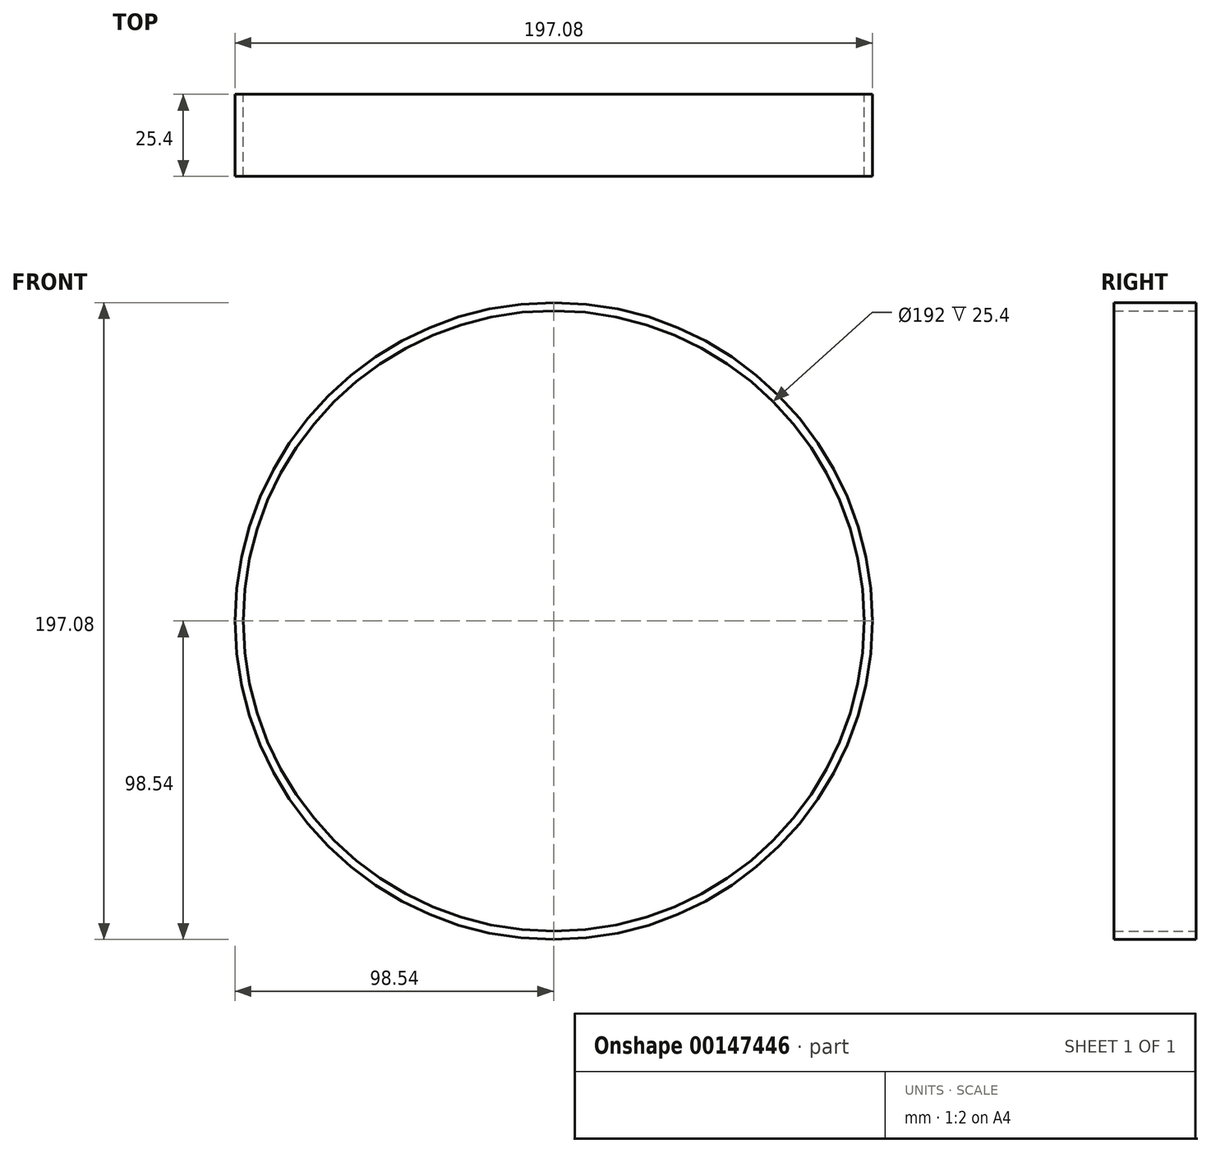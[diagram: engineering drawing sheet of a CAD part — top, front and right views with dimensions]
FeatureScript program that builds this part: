
annotation { "Feature Type Name" : "Feature", "Feature Type Description" : "" }
export const myFeature = defineFeature(function(context is Context, id is Id, definition is map)
    precondition{}
    {
        {
            var Q0;
            Q0=qCreatedBy(makeId("Front.planeOp"),FACE);
            var sketch = newSketch(context, id + "F0", { "sketchPlane" : qUnion([Q0])});
            skCircle(sketch, "E0", {"center": v(0, 0) * mm, "radius": 79.1 * mm});
            skCircle(sketch, "E1", {"center": v(0, 0) * mm, "radius": 98.54 * mm});
            skSolve(sketch);
        }
        {
            var Q0;
            Q0=makeQuery(id+"F0.imprint","IMPRINT",FACE,{"disambiguationData":[TD([[makeQuery(id+"F0.imprint","IMPRINT",EDGE,{"derivedFrom":sQuery(id+"F0.wireOp",EDGE,"E0")}),1.0]])]});
            var Q1;
            Q1=makeQuery(id+"F0.imprint","IMPRINT",FACE,{"disambiguationData":[TD([[makeQuery(id+"F0.imprint","IMPRINT",EDGE,{"derivedFrom":sQuery(id+"F0.wireOp",EDGE,"E0")}),-1.0]])]});
            extrude(context, id + "F1", {"entities" : qUnion([Q0, Q1]), "depth" : 25.4 * mm});
        }
        {
            var Q0;
            Q0=makeQuery(id+"F1.opExtrude","CAP_FACE",FACE,{"disambiguationData":[OSD([sQuery(id+"F0.wireOp",EDGE,"E1")])],"isStart":false});
            var Q1;
            Q1=makeQuery(id+"F1.opExtrude","CAP_FACE",FACE,{"disambiguationData":[OSD([sQuery(id+"F0.wireOp",EDGE,"E1")])],"isStart":true});
            shell(context, id + "F2", {"entities" : qUnion([Q0, Q1]), "thickness" : 2.54 * mm});
        }
    });
